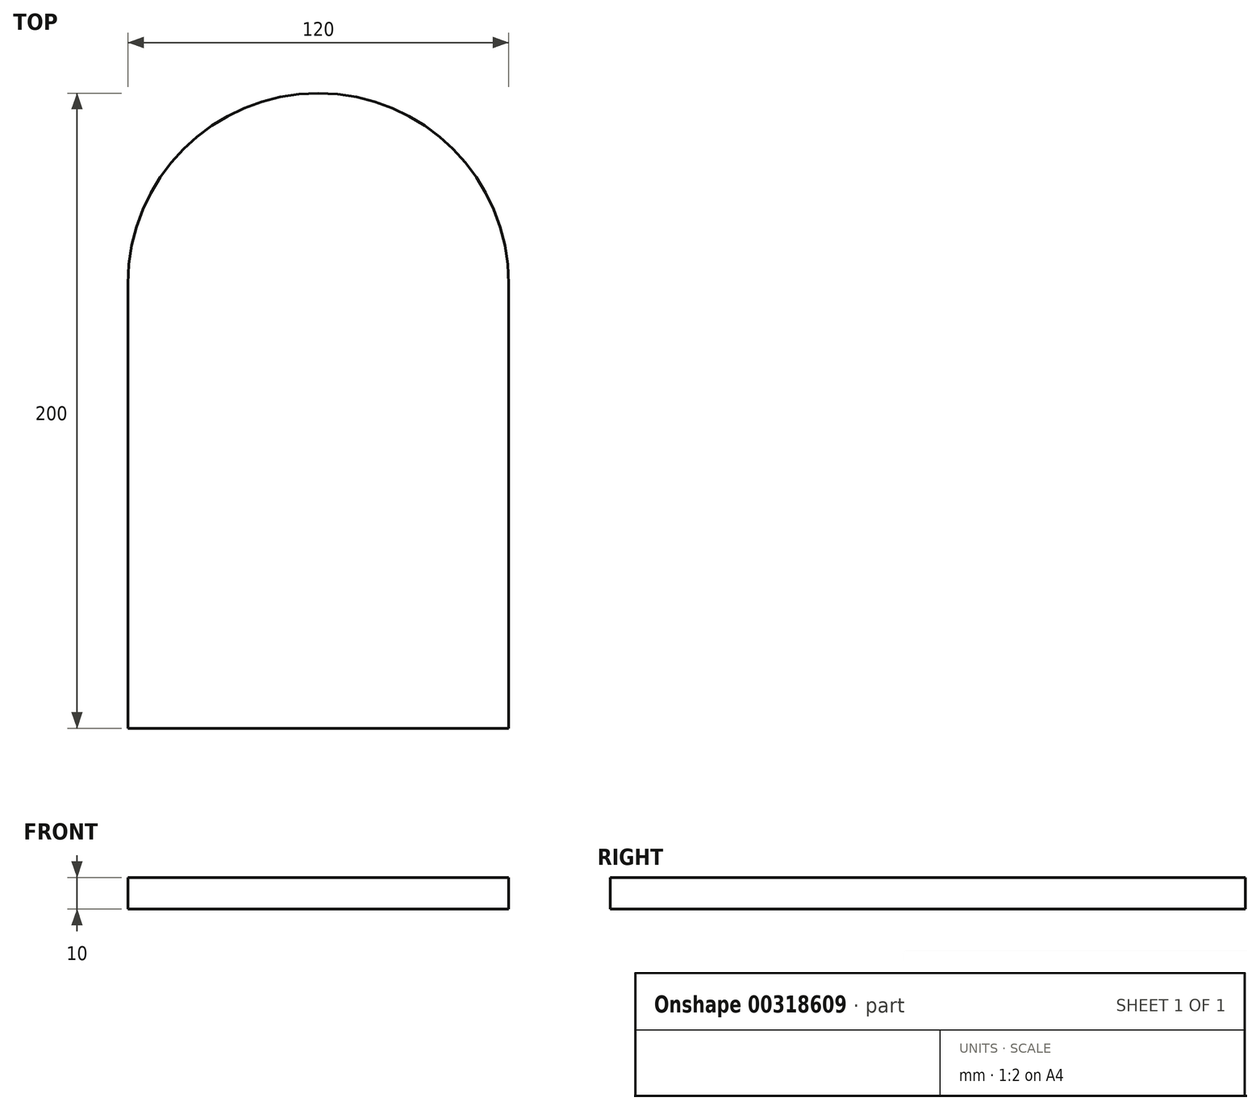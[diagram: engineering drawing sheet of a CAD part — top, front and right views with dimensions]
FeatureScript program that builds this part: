
annotation { "Feature Type Name" : "Feature", "Feature Type Description" : "" }
export const myFeature = defineFeature(function(context is Context, id is Id, definition is map)
    precondition{}
    {
        {
            var Q0;
            Q0=qCreatedBy(makeId("Top.planeOp"),FACE);
            var sketch = newSketch(context, id + "F0", { "sketchPlane" : qUnion([Q0])});
            skLineSegment(sketch, "E0", {"start": v(-60, 0) * mm, "end": v(60, 0) * mm});
            skLineSegment(sketch, "E1", {"start": v(60, 0) * mm, "end": v(60, 140) * mm});
            skLineSegment(sketch, "E2", {"start": v(-60, 140) * mm, "end": v(-60, 0) * mm});
            skArc(sketch, "E3", {"start": v(-60, 140) * mm, "mid": v(0, 200) * mm, "end": v(60, 140) * mm});
            skSolve(sketch);
        }
        {
            var Q0;
            Q0 = qSketchRegion(id + "F0", true);
            extrude(context, id + "F1", {"entities" : qUnion([Q0]), "depth" : 10 * mm});
        }
    });
